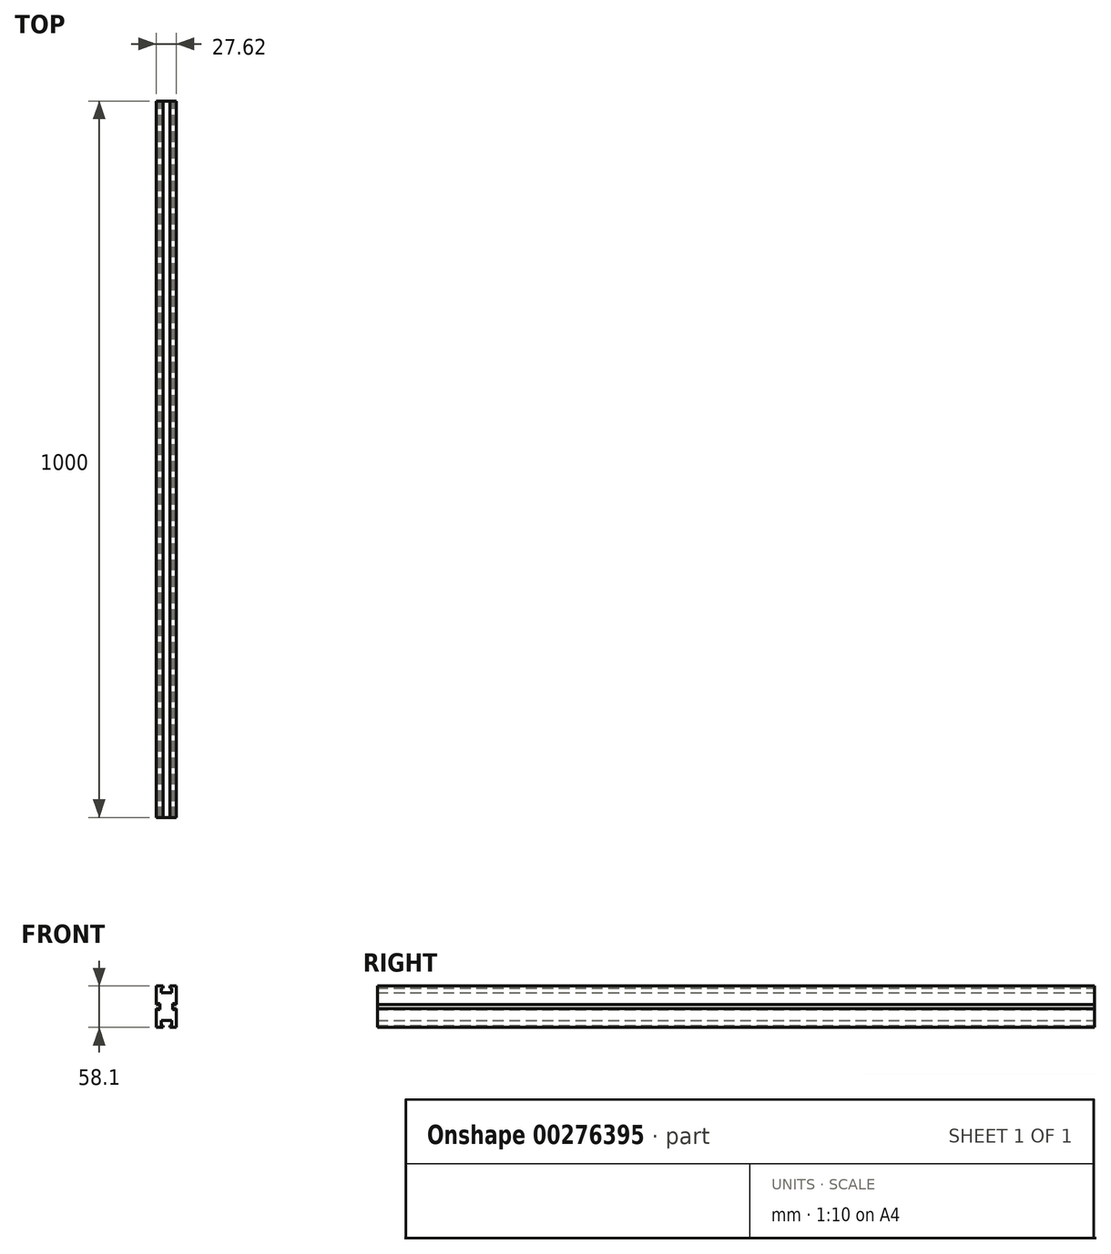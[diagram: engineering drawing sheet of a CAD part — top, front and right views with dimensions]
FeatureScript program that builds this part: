
annotation { "Feature Type Name" : "Feature", "Feature Type Description" : "" }
export const myFeature = defineFeature(function(context is Context, id is Id, definition is map)
    precondition{}
    {
        {
            assignVariable(context, id + "F0", {"name" : "Length", "anyValue" : 1000});
        }
        {
            var Q0;
            Q0=qCreatedBy(makeId("Front.planeOp"),FACE);
            var sketch = newSketch(context, id + "F1", { "sketchPlane" : qUnion([Q0])});
            skLineSegment(sketch, "E0", {"start": v(0, 19.53) * mm, "end": v(-7.32, 19.53) * mm});
            skLineSegment(sketch, "E1", {"start": v(-7.32, 19.53) * mm, "end": v(-7.32, 26.04) * mm});
            skLineSegment(sketch, "E2", {"start": v(-7.32, 26.04) * mm, "end": v(-4.78, 26.04) * mm});
            skLineSegment(sketch, "E3", {"start": v(-4.78, 26.04) * mm, "end": v(-4.78, 29.05) * mm});
            skLineSegment(sketch, "E4", {"start": v(-4.78, 29.05) * mm, "end": v(-13.81, 29.05) * mm});
            skLineSegment(sketch, "E5", {"start": v(-13.81, 29.05) * mm, "end": v(-13.81, 2.76) * mm});
            skLineSegment(sketch, "E6", {"start": v(-13.81, 2.76) * mm, "end": v(-11.4, 2.76) * mm});
            skLineSegment(sketch, "E7", {"start": v(-11.4, 2.76) * mm, "end": v(-11.4, 4.21) * mm});
            skLineSegment(sketch, "E8", {"start": v(-11.4, 4.21) * mm, "end": v(-8.81, 4.21) * mm});
            skLineSegment(sketch, "E9", {"start": v(-8.81, 4.21) * mm, "end": v(-8.81, 0) * mm});
            skLineSegment(sketch, "E10.MirrorCS", {"start": v(13.81, 2.76) * mm, "end": v(11.4, 2.76) * mm});
            skLineSegment(sketch, "E11.MirrorCS", {"start": v(4.78, 26.04) * mm, "end": v(4.78, 29.05) * mm});
            skLineSegment(sketch, "E12.MirrorCS", {"start": v(7.32, 26.04) * mm, "end": v(4.78, 26.04) * mm});
            skLineSegment(sketch, "E13.MirrorCS", {"start": v(11.4, 2.76) * mm, "end": v(11.4, 4.21) * mm});
            skLineSegment(sketch, "E14.MirrorCS", {"start": v(11.4, 4.21) * mm, "end": v(8.81, 4.21) * mm});
            skLineSegment(sketch, "E15.MirrorCS", {"start": v(4.78, 29.05) * mm, "end": v(13.81, 29.05) * mm});
            skLineSegment(sketch, "E16.MirrorCS", {"start": v(13.81, 29.05) * mm, "end": v(13.81, 2.76) * mm});
            skLineSegment(sketch, "E17.MirrorCS", {"start": v(7.32, 19.53) * mm, "end": v(7.32, 26.04) * mm});
            skLineSegment(sketch, "E18.MirrorCS", {"start": v(0, 19.53) * mm, "end": v(7.32, 19.53) * mm});
            skLineSegment(sketch, "E19.MirrorCS", {"start": v(8.81, 4.21) * mm, "end": v(8.81, 0) * mm});
            skLineSegment(sketch, "E20.MirrorCS", {"start": v(4.78, -26.04) * mm, "end": v(4.78, -29.05) * mm});
            skLineSegment(sketch, "E21.MirrorCS", {"start": v(7.32, -26.04) * mm, "end": v(4.78, -26.04) * mm});
            skLineSegment(sketch, "E22.MirrorCS", {"start": v(11.4, -2.76) * mm, "end": v(11.4, -4.21) * mm});
            skLineSegment(sketch, "E23.MirrorCS", {"start": v(8.81, -4.21) * mm, "end": v(8.81, 0) * mm});
            skLineSegment(sketch, "E24.MirrorCS", {"start": v(-7.32, -26.04) * mm, "end": v(-4.78, -26.04) * mm});
            skLineSegment(sketch, "E25.MirrorCS", {"start": v(-4.78, -26.04) * mm, "end": v(-4.78, -29.05) * mm});
            skLineSegment(sketch, "E26.MirrorCS", {"start": v(-11.4, -2.76) * mm, "end": v(-11.4, -4.21) * mm});
            skLineSegment(sketch, "E27.MirrorCS", {"start": v(-13.81, -2.76) * mm, "end": v(-11.4, -2.76) * mm});
            skLineSegment(sketch, "E28.MirrorCS", {"start": v(11.4, -4.21) * mm, "end": v(8.81, -4.21) * mm});
            skLineSegment(sketch, "E29.MirrorCS", {"start": v(-11.4, -4.21) * mm, "end": v(-8.81, -4.21) * mm});
            skLineSegment(sketch, "E30.MirrorCS", {"start": v(-8.81, -4.21) * mm, "end": v(-8.81, 0) * mm});
            skLineSegment(sketch, "E31.MirrorCS", {"start": v(13.81, -2.76) * mm, "end": v(11.4, -2.76) * mm});
            skLineSegment(sketch, "E32.MirrorCS", {"start": v(0, -19.53) * mm, "end": v(-7.32, -19.53) * mm});
            skLineSegment(sketch, "E33.MirrorCS", {"start": v(0, -19.53) * mm, "end": v(7.32, -19.53) * mm});
            skLineSegment(sketch, "E34.MirrorCS", {"start": v(-7.32, -19.53) * mm, "end": v(-7.32, -26.04) * mm});
            skLineSegment(sketch, "E35.MirrorCS", {"start": v(7.32, -19.53) * mm, "end": v(7.32, -26.04) * mm});
            skLineSegment(sketch, "E36.MirrorCS", {"start": v(13.81, -29.05) * mm, "end": v(13.81, -2.76) * mm});
            skLineSegment(sketch, "E37.MirrorCS", {"start": v(-4.78, -29.05) * mm, "end": v(-13.81, -29.05) * mm});
            skLineSegment(sketch, "E38.MirrorCS", {"start": v(-13.81, -29.05) * mm, "end": v(-13.81, -2.76) * mm});
            skLineSegment(sketch, "E39.MirrorCS", {"start": v(4.78, -29.05) * mm, "end": v(13.81, -29.05) * mm});
            skSolve(sketch);
        }
        {
            var Q0;
            Q0 = qSketchRegion(id + "F1", true);
            extrude(context, id + "F2", {"entities" : qUnion([Q0]), "depth" : getVariable(context, 'Length') * mm});
        }
    });
